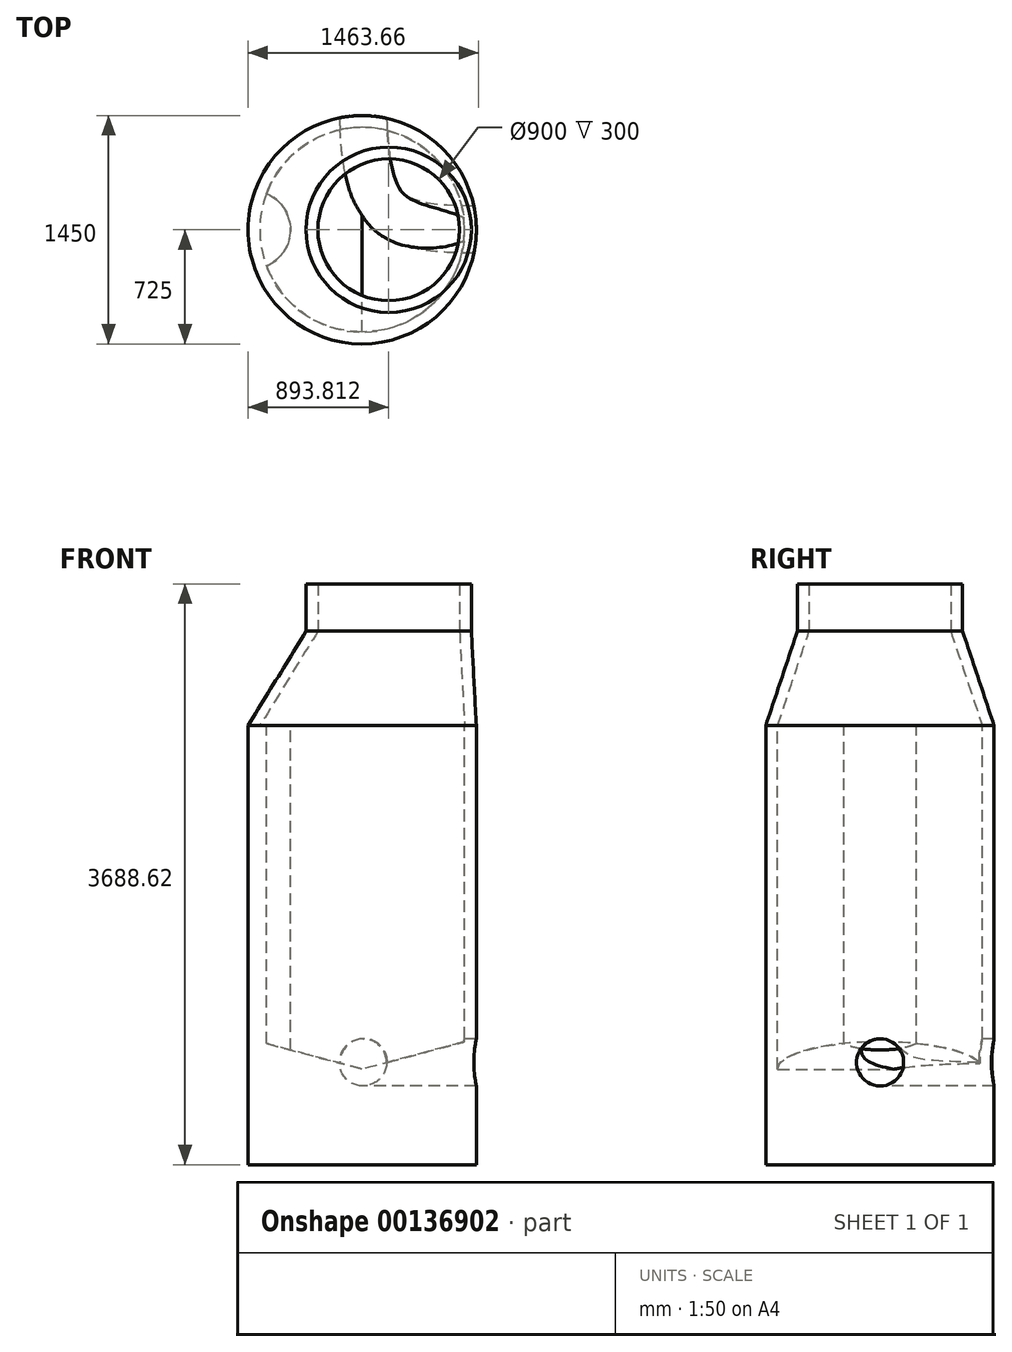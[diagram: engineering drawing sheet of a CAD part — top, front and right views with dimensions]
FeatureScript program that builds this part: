
annotation { "Feature Type Name" : "Feature", "Feature Type Description" : "" }
export const myFeature = defineFeature(function(context is Context, id is Id, definition is map)
    precondition{}
    {
        {
            var Q0;
            Q0=qCreatedBy(makeId("Top.planeOp"),FACE);
            var sketch = newSketch(context, id + "F0", { "sketchPlane" : qUnion([Q0])});
            skCircle(sketch, "E0", {"center": v(0, 0) * mm, "radius": 725 * mm});
            skSolve(sketch);
        }
        {
            var Q0;
            Q0=makeQuery(id+"F0.imprint","IMPRINT",FACE,{"disambiguationData":[TD([[makeQuery(id+"F0.imprint","IMPRINT",EDGE,{"derivedFrom":sQuery(id+"F0.wireOp",EDGE,"E0")}),1.0]])]});
            cPlane(context, id + "F1", {"entities" : qUnion([Q0]), "cplaneType" : CPlaneType.OFFSET, "offset" : 600 * mm, "width" : 150 * mm, "height" : 150 * mm});
        }
        {
            var Q0;
            Q0=qCreatedBy(id+"F1.planeOp",FACE);
            var sketch = newSketch(context, id + "F2", { "sketchPlane" : qUnion([Q0])});
            skCircle(sketch, "E1", {"center": v(168.81, 0) * mm, "radius": 525 * mm});
            skSolve(sketch);
        }
        {
            var Q0;
            Q0=makeQuery(id+"F2.imprint","IMPRINT",FACE,{"disambiguationData":[TD([[makeQuery(id+"F2.imprint","IMPRINT",EDGE,{"derivedFrom":sQuery(id+"F2.wireOp",EDGE,"E1")}),1.0]])]});
            var Q1;
            Q1=makeQuery(id+"F0.imprint","IMPRINT",FACE,{"disambiguationData":[TD([[makeQuery(id+"F0.imprint","IMPRINT",EDGE,{"derivedFrom":sQuery(id+"F0.wireOp",EDGE,"E0")}),1.0]])]});
            loft(context, id + "F3", {"sheetProfilesArray" : [{ "sheetProfileEntities" : qUnion([Q0]) }, { "sheetProfileEntities" : qUnion([Q1]) }]});
        }
        {
            var Q0;
            Q0=makeQuery(id+"F3.opLoft","CAP_FACE",FACE,{"disambiguationData":[OSD([makeQuery(id+"F2.imprint","IMPRINT",FACE,{"disambiguationData":[TD([[makeQuery(id+"F2.imprint","IMPRINT",EDGE,{"derivedFrom":sQuery(id+"F2.wireOp",EDGE,"E1")}),1.0]])]})])],"isStart":true});
            var sketch = newSketch(context, id + "F4", { "sketchPlane" : qUnion([Q0])});
            skCircle(sketch, "E2", {"center": v(168.81, 0) * mm, "radius": 450 * mm});
            skSolve(sketch);
        }
        {
            var Q0;
            Q0=makeQuery(id+"F3.opLoft","CAP_FACE",FACE,{"disambiguationData":[OSD([makeQuery(id+"F0.imprint","IMPRINT",FACE,{"disambiguationData":[TD([[makeQuery(id+"F0.imprint","IMPRINT",EDGE,{"derivedFrom":sQuery(id+"F0.wireOp",EDGE,"E0")}),1.0]])]})])],"isStart":true});
            var sketch = newSketch(context, id + "F5", { "sketchPlane" : qUnion([Q0])});
            skCircle(sketch, "E3", {"center": v(0, 0) * mm, "radius": 650 * mm});
            skSolve(sketch);
        }
        {
            var Q1;
            Q1=makeQuery(id+"F4.imprint","IMPRINT",FACE,{"disambiguationData":[TD([[makeQuery(id+"F4.imprint","IMPRINT",EDGE,{"derivedFrom":sQuery(id+"F4.wireOp",EDGE,"E2")}),1.0]])]});
            var Q2;
            Q2=makeQuery(id+"F5.imprint","IMPRINT",FACE,{"disambiguationData":[TD([[makeQuery(id+"F5.imprint","IMPRINT",EDGE,{"derivedFrom":sQuery(id+"F5.wireOp",EDGE,"E3")}),1.0]])]});
            loft(context, id + "F6", {"operationType" : NewBodyOperationType.REMOVE, "sheetProfilesArray" : [{ "sheetProfileEntities" : qUnion([Q1]) }, { "sheetProfileEntities" : qUnion([Q2]) }]});
        }
        {
            var Q0;
            Q0=makeQuery(id+"F3.opLoft","CAP_FACE",FACE,{"disambiguationData":[OSD([makeQuery(id+"F2.imprint","IMPRINT",FACE,{"disambiguationData":[TD([[makeQuery(id+"F2.imprint","IMPRINT",EDGE,{"derivedFrom":sQuery(id+"F2.wireOp",EDGE,"E1")}),1.0]])]})])],"isStart":true});
            extrude(context, id + "F7", {"entities" : qUnion([Q0]), "operationType" : NewBodyOperationType.ADD, "depth" : 300 * mm});
        }
        {
            var Q0;
            Q0=makeQuery(id+"F3.opLoft","CAP_FACE",FACE,{"disambiguationData":[OSD([makeQuery(id+"F0.imprint","IMPRINT",FACE,{"disambiguationData":[TD([[makeQuery(id+"F0.imprint","IMPRINT",EDGE,{"derivedFrom":sQuery(id+"F0.wireOp",EDGE,"E0")}),1.0]])]})])],"isStart":true});
            extrude(context, id + "F8", {"entities" : qUnion([Q0]), "operationType" : NewBodyOperationType.ADD, "depth" : 2500 * mm});
        }
        {
            var Q0;
            Q0=qCreatedBy(makeId("Front.planeOp"),FACE);
            var sketch = newSketch(context, id + "F9", { "sketchPlane" : qUnion([Q0])});
            skLineSegment(sketch, "E4", {"start": v(0, -2181.9) * mm, "end": v(-857.7, -1952.1) * mm});
            skLineSegment(sketch, "E5", {"start": v(-857.7, -1952.1) * mm, "end": v(-857.7, -2788.62) * mm});
            skLineSegment(sketch, "E6", {"start": v(-857.7, -2788.62) * mm, "end": v(857.7, -2788.62) * mm});
            skLineSegment(sketch, "E7", {"start": v(857.7, -2788.62) * mm, "end": v(857.7, -1952.1) * mm});
            skLineSegment(sketch, "E8", {"start": v(857.7, -1952.1) * mm, "end": v(0, -2181.9) * mm});
            skSolve(sketch);
        }
        {
            var Q0;
            Q0=makeQuery(id+"F9.imprint","IMPRINT",FACE,{"disambiguationData":[TD([[makeQuery(id+"F9.imprint","IMPRINT",EDGE,{"derivedFrom":sQuery(id+"F9.wireOp",EDGE,"E4")}),1.0]])]});
            extrude(context, id + "F10", {"entities" : qUnion([Q0]), "operationType" : NewBodyOperationType.ADD, "endBound" : BoundingType.SYMMETRIC, "depth" : 1500 * mm});
        }
        {
            var Q0;
            Q0=qCreatedBy(makeId("Top.planeOp"),FACE);
            var sketch = newSketch(context, id + "F11", { "sketchPlane" : qUnion([Q0])});
            skCircle(sketch, "E9", {"center": v(0, 0) * mm, "radius": 725 * mm});
            skLineSegment(sketch, "E10.bottom", {"start": v(-1044.1, 812.44) * mm, "end": v(1170.08, 812.44) * mm});
            skLineSegment(sketch, "E10.top", {"start": v(-1044.1, -954.59) * mm, "end": v(1170.08, -954.59) * mm});
            skLineSegment(sketch, "E10.left", {"start": v(-1044.1, 812.44) * mm, "end": v(-1044.1, -954.59) * mm});
            skLineSegment(sketch, "E10.right", {"start": v(1170.08, 812.44) * mm, "end": v(1170.08, -954.59) * mm});
            skSolve(sketch);
        }
        {
            var Q0;
            Q0=makeQuery(id+"F11.imprint","IMPRINT",FACE,{"disambiguationData":[TD([[makeQuery(id+"F11.imprint","IMPRINT",EDGE,{"derivedFrom":sQuery(id+"F11.wireOp",EDGE,"E9")}),-1.0]])]});
            extrude(context, id + "F12", {"entities" : qUnion([Q0]), "operationType" : NewBodyOperationType.REMOVE, "oppositeDirection" : true, "depth" : 3000 * mm});
        }
        {
            var Q0;
            Q0=makeQuery(id+"F10.opExtrude","SWEPT_FACE",FACE,{"disambiguationData":[OSD([sQuery(id+"F9.wireOp",EDGE,"E6")])]});
            cPlane(context, id + "F13", {"entities" : qUnion([Q0]), "cplaneType" : CPlaneType.OFFSET, "offset" : 650 * mm, "oppositeDirection" : true, "width" : 150 * mm, "height" : 150 * mm});
        }
        {
            var Q0;
            Q0=qCreatedBy(id+"F13.planeOp",FACE);
            var sketch = newSketch(context, id + "F14", { "sketchPlane" : qUnion([Q0])});
            skFitSpline(sketch, "E11", {"points": [v(0, -800) * mm, v(150.15, -132.55) * mm, v(800, 0) * mm], "startDerivative": vector(88.16, 1345.18) * mm, "endDerivative": vector(1493, 26.17) * mm});
            skSolve(sketch);
        }
        {
            var Q0;
            Q0=qCreatedBy(makeId("Front.planeOp"),FACE);
            cPlane(context, id + "F15", {"entities" : qUnion([Q0]), "cplaneType" : CPlaneType.OFFSET, "offset" : 800 * mm, "oppositeDirection" : true, "width" : 150 * mm, "height" : 150 * mm});
        }
        {
            var Q0;
            Q0=qCreatedBy(id+"F15.planeOp",FACE);
            var sketch = newSketch(context, id + "F16", { "sketchPlane" : qUnion([Q0])});
            skCircle(sketch, "E12", {"center": v(0, -2138.85) * mm, "radius": 150 * mm});
            skSolve(sketch);
        }
        {
            var Q0;
            Q0=makeQuery(id+"F16.imprint","IMPRINT",FACE,{"disambiguationData":[TD([[makeQuery(id+"F16.imprint","IMPRINT",EDGE,{"derivedFrom":sQuery(id+"F16.wireOp",EDGE,"E12")}),1.0]])]});
            var Q1;
            Q1=sQuery(id+"F14.wireOp",EDGE,"E11");
            sweep(context, id + "F17", {"operationType" : NewBodyOperationType.REMOVE, "profiles" : qUnion([Q0]), "path" : qUnion([Q1])});
        }
        {
            var Q0;
            Q0=qCreatedBy(makeId("Top.planeOp"),FACE);
            var sketch = newSketch(context, id + "F18", { "sketchPlane" : qUnion([Q0])});
            skCircle(sketch, "E13", {"center": v(-705.22, 0) * mm, "radius": 250 * mm});
            skSolve(sketch);
        }
        {
            var Q0;
            Q0=makeQuery(id+"F18.imprint","IMPRINT",FACE,{"disambiguationData":[TD([[makeQuery(id+"F18.imprint","IMPRINT",EDGE,{"derivedFrom":sQuery(id+"F18.wireOp",EDGE,"E13")}),1.0]])]});
            extrude(context, id + "F19", {"entities" : qUnion([Q0]), "operationType" : NewBodyOperationType.ADD, "oppositeDirection" : true, "depth" : 2500 * mm});
        }
        {
            var Q0;
            Q0 = qSketchRegion(id + "F11", true);
            extrude(context, id + "F20", {"entities" : qUnion([Q0]), "operationType" : NewBodyOperationType.REMOVE, "oppositeDirection" : true, "depth" : 2500 * mm});
        }
    });
